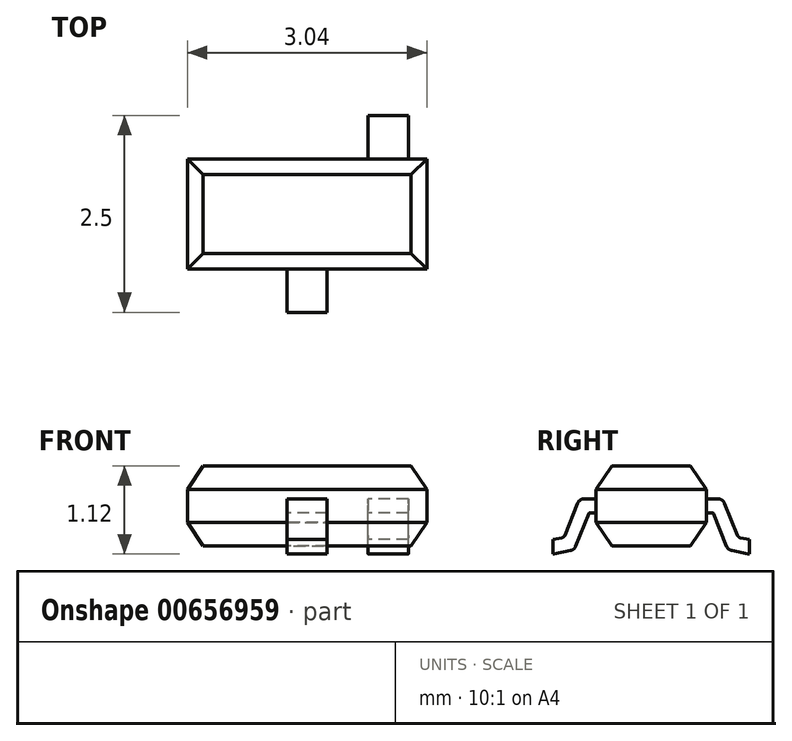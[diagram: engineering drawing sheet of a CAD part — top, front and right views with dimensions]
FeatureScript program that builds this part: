
annotation { "Feature Type Name" : "Feature", "Feature Type Description" : "" }
export const myFeature = defineFeature(function(context is Context, id is Id, definition is map)
    precondition{}
    {
        {
            var Q0;
            Q0=qCreatedBy(makeId("Top.planeOp"),FACE);
            cPlane(context, id + "F0", {"entities" : qUnion([Q0]), "cplaneType" : CPlaneType.OFFSET, "offset" : 0.1 * mm, "width" : 150 * mm, "height" : 150 * mm});
        }
        {
            var Q0;
            Q0=qCreatedBy(id+"F0.planeOp",FACE);
            var sketch = newSketch(context, id + "F1", { "sketchPlane" : qUnion([Q0])});
            skLineSegment(sketch, "E0.bottom", {"start": v(-1.52, 0.7) * mm, "end": v(1.52, 0.7) * mm});
            skLineSegment(sketch, "E0.top", {"start": v(-1.52, -0.7) * mm, "end": v(1.52, -0.7) * mm});
            skLineSegment(sketch, "E0.left", {"start": v(-1.52, 0.7) * mm, "end": v(-1.52, -0.7) * mm});
            skLineSegment(sketch, "E0.right", {"start": v(1.52, 0.7) * mm, "end": v(1.52, -0.7) * mm});
            skPoint(sketch, "E0.middle", {"position": v(0, 0) * mm});
            skSolve(sketch);
        }
        {
            var Q0;
            Q0=makeQuery(id+"F1.imprint","IMPRINT",FACE,{"disambiguationData":[TD([[makeQuery(id+"F1.imprint","IMPRINT",EDGE,{"derivedFrom":sQuery(id+"F1.wireOp",EDGE,"E0.bottom")}),-1.0]])]});
            extrude(context, id + "F2", {"entities" : qUnion([Q0]), "depth" : 1.02 * mm, "offsetDistance" : 25 * mm});
        }
        {
            var Q0;
            Q0=makeQuery(id+"F2.opExtrude","CAP_EDGE",EDGE,{"disambiguationData":[OSD([sQuery(id+"F1.wireOp",EDGE,"E0.left")])],"isStart":false});
            var Q1;
            Q1=makeQuery(id+"F2.opExtrude","CAP_EDGE",EDGE,{"disambiguationData":[OSD([sQuery(id+"F1.wireOp",EDGE,"E0.left")])],"isStart":true});
            var Q2;
            Q2=makeQuery(id+"F2.opExtrude","CAP_EDGE",EDGE,{"disambiguationData":[OSD([sQuery(id+"F1.wireOp",EDGE,"E0.right")])],"isStart":true});
            var Q3;
            Q3=makeQuery(id+"F2.opExtrude","CAP_EDGE",EDGE,{"disambiguationData":[OSD([sQuery(id+"F1.wireOp",EDGE,"E0.right")])],"isStart":false});
            chamfer(context, id + "F3", {"entities" : qUnion([Q0, Q1, Q2, Q3]), "chamferType" : ChamferType.TWO_OFFSETS, "width1" : 0.2 * mm, "oppositeDirection" : false, "width2" : 0.3 * mm, "tangentPropagation" : true});
        }
        {
            var Q0;
            Q0=makeQuery(id+"F2.opExtrude","CAP_EDGE",EDGE,{"disambiguationData":[OSD([sQuery(id+"F1.wireOp",EDGE,"E0.top")])],"isStart":false});
            var Q1;
            Q1=makeQuery(id+"F2.opExtrude","CAP_EDGE",EDGE,{"disambiguationData":[OSD([sQuery(id+"F1.wireOp",EDGE,"E0.top")])],"isStart":true});
            var Q2;
            Q2=makeQuery(id+"F2.opExtrude","CAP_EDGE",EDGE,{"disambiguationData":[OSD([sQuery(id+"F1.wireOp",EDGE,"E0.bottom")])],"isStart":true});
            var Q3;
            Q3=makeQuery(id+"F2.opExtrude","CAP_EDGE",EDGE,{"disambiguationData":[OSD([sQuery(id+"F1.wireOp",EDGE,"E0.bottom")])],"isStart":false});
            chamfer(context, id + "F4", {"entities" : qUnion([Q0, Q1, Q2, Q3]), "chamferType" : ChamferType.TWO_OFFSETS, "width1" : 0.2 * mm, "oppositeDirection" : false, "width2" : 0.3 * mm, "tangentPropagation" : true});
        }
        {
            var Q0;
            {var subQ0=sQuery(id+"F1.wireOp",EDGE,"E0.top");Q0=makeQuery(id+"F4.opChamfer","BLEND_EDGE",EDGE,{"blendedFrom":[makeQuery(id+"F2.opExtrude","CAP_EDGE",EDGE,{"disambiguationData":[OSD([subQ0])],"isStart":false}),makeQuery(id+"F2.opExtrude","CAP_FACE",FACE,{"disambiguationData":[OSD([sQuery(id+"F1.wireOp",EDGE,"E0.bottom"),subQ0,sQuery(id+"F1.wireOp",EDGE,"E0.left"),sQuery(id+"F1.wireOp",EDGE,"E0.right")])],"isStart":false})],"blendedInto":[makeQuery(id+"F2.opExtrude","CAP_FACE",FACE,{"disambiguationData":[OSD([sQuery(id+"F1.wireOp",EDGE,"E0.bottom"),subQ0,sQuery(id+"F1.wireOp",EDGE,"E0.left"),sQuery(id+"F1.wireOp",EDGE,"E0.right")])],"isStart":false})]});}
            cPoint(context, id + "F5", {"entities" : qUnion([Q0]), "parameter" : 0.5});
        }
        {
            var Q0;
            {var subQ0=sQuery(id+"F1.wireOp",EDGE,"E0.bottom");Q0=makeQuery(id+"F4.opChamfer","BLEND_EDGE",EDGE,{"blendedFrom":[makeQuery(id+"F2.opExtrude","CAP_EDGE",EDGE,{"disambiguationData":[OSD([subQ0])],"isStart":false}),makeQuery(id+"F2.opExtrude","CAP_FACE",FACE,{"disambiguationData":[OSD([subQ0,sQuery(id+"F1.wireOp",EDGE,"E0.top"),sQuery(id+"F1.wireOp",EDGE,"E0.left"),sQuery(id+"F1.wireOp",EDGE,"E0.right")])],"isStart":false})],"blendedInto":[makeQuery(id+"F2.opExtrude","CAP_FACE",FACE,{"disambiguationData":[OSD([subQ0,sQuery(id+"F1.wireOp",EDGE,"E0.top"),sQuery(id+"F1.wireOp",EDGE,"E0.left"),sQuery(id+"F1.wireOp",EDGE,"E0.right")])],"isStart":false})]});}
            cPoint(context, id + "F6", {"entities" : qUnion([Q0]), "parameter" : 0.5});
        }
        {
            var Q0;
            {var subQ0=sQuery(id+"F1.wireOp",EDGE,"E0.bottom");Q0=makeQuery(id+"F4.opChamfer","BLEND_EDGE",EDGE,{"blendedFrom":[makeQuery(id+"F2.opExtrude","CAP_EDGE",EDGE,{"disambiguationData":[OSD([subQ0])],"isStart":true}),makeQuery(id+"F2.opExtrude","CAP_FACE",FACE,{"disambiguationData":[OSD([subQ0,sQuery(id+"F1.wireOp",EDGE,"E0.top"),sQuery(id+"F1.wireOp",EDGE,"E0.left"),sQuery(id+"F1.wireOp",EDGE,"E0.right")])],"isStart":true})],"blendedInto":[makeQuery(id+"F2.opExtrude","CAP_FACE",FACE,{"disambiguationData":[OSD([subQ0,sQuery(id+"F1.wireOp",EDGE,"E0.top"),sQuery(id+"F1.wireOp",EDGE,"E0.left"),sQuery(id+"F1.wireOp",EDGE,"E0.right")])],"isStart":true})]});}
            cPoint(context, id + "F7", {"entities" : qUnion([Q0]), "parameter" : 0.5});
        }
        {
            var Q0;
            Q0=qCreatedBy(id+"F5",VERTEX);
            var Q1;
            Q1=qCreatedBy(id+"F6",VERTEX);
            var Q2;
            Q2=qCreatedBy(id+"F7",VERTEX);
            cPlane(context, id + "F8", {"entities" : qUnion([Q0, Q1, Q2]), "cplaneType" : CPlaneType.THREE_POINT, "offset" : 25 * mm, "width" : 150 * mm, "height" : 150 * mm});
        }
        {
            var Q0;
            Q0=qCreatedBy(id+"F8.planeOp",FACE);
            var sketch = newSketch(context, id + "F9", { "sketchPlane" : qUnion([Q0])});
            skLineSegment(sketch, "E1", {"start": v(0, 0) * mm, "end": v(-2.5, 0) * mm, "construction": true});
            skLineSegment(sketch, "E2", {"start": v(-1.25, 0) * mm, "end": v(-1.25, 0.09) * mm});
            skLineSegment(sketch, "E3", {"start": v(-0.7, 0.61) * mm, "end": v(-0.85, 0.61) * mm, "construction": true});
            skLineSegment(sketch, "E4", {"start": v(-1.04, 0.13) * mm, "end": v(-0.85, 0.61) * mm, "construction": true});
            skArc(sketch, "E5.0.startCap", {"start": v(-0.96, 0.1) * mm, "mid": v(-0.98, 0.06) * mm, "end": v(-1.02, 0.04) * mm});
            skArc(sketch, "E5.0.endCap", {"start": v(-0.93, 0.64) * mm, "mid": v(-0.9, 0.68) * mm, "end": v(-0.85, 0.7) * mm});
            skLineSegment(sketch, "E5.0.left", {"start": v(-1.1, 0.24) * mm, "end": v(-0.93, 0.64) * mm});
            skLineSegment(sketch, "E5.0.right", {"start": v(-0.96, 0.1) * mm, "end": v(-0.8, 0.51) * mm});
            skArc(sketch, "E6.0.startCap", {"start": v(-1.23, 0) * mm, "mid": v(-1.24, 0) * mm, "end": v(-1.25, 0) * mm});
            skLineSegment(sketch, "E6.0.left", {"start": v(-1.25, 0.18) * mm, "end": v(-1.13, 0.2) * mm});
            skLineSegment(sketch, "E6.0.right", {"start": v(-1.23, 0) * mm, "end": v(-1.02, 0.04) * mm});
            skLineSegment(sketch, "E6.1.left", {"start": v(-0.7, 0.52) * mm, "end": v(-0.78, 0.52) * mm});
            skLineSegment(sketch, "E6.1.right", {"start": v(-0.7, 0.7) * mm, "end": v(-0.85, 0.7) * mm});
            skLineSegment(sketch, "E7", {"start": v(-0.7, 0.7) * mm, "end": v(-0.7, 0.52) * mm});
            skLineSegment(sketch, "E8", {"start": v(-1.25, 0.18) * mm, "end": v(-1.25, 0.18) * mm});
            skLineSegment(sketch, "E9.trimOffspring", {"start": v(-1.25, 0.09) * mm, "end": v(-1.25, 0) * mm});
            skLineSegment(sketch, "E10", {"start": v(-1.25, 0.09) * mm, "end": v(-1.25, 0.18) * mm});
            skPoint(sketch, "E11.visualSharp", {"position": v(-0.79, 0.52) * mm});
            skArc(sketch, "E11.filletArc", {"start": v(-0.78, 0.52) * mm, "mid": v(-0.79, 0.52) * mm, "end": v(-0.8, 0.51) * mm});
            skPoint(sketch, "E12.visualSharp", {"position": v(-1.1, 0.21) * mm});
            skArc(sketch, "E12.filletArc", {"start": v(-1.13, 0.2) * mm, "mid": v(-1.11, 0.22) * mm, "end": v(-1.1, 0.24) * mm});
            skSolve(sketch);
        }
        {
            var Q0;
            Q0=makeQuery(id+"F9.imprint","IMPRINT",FACE,{"disambiguationData":[TD([[makeQuery(id+"F9.imprint","IMPRINT",EDGE,{"derivedFrom":sQuery(id+"F9.wireOp",EDGE,"E5.0.left")}),-1.0]])]});
            extrude(context, id + "F10", {"entities" : qUnion([Q0]), "operationType" : NewBodyOperationType.ADD, "endBound" : BoundingType.SYMMETRIC, "depth" : 0.51 * mm, "offsetDistance" : 25 * mm});
        }
        {
            var Q0;
            Q0=qCreatedBy(id+"F8.planeOp",FACE);
            cPlane(context, id + "F11", {"entities" : qUnion([Q0]), "cplaneType" : CPlaneType.OFFSET, "offset" : 1.03 * mm, "width" : 150 * mm, "height" : 150 * mm});
        }
        {
            var Q0;
            Q0=qCreatedBy(id+"F11.planeOp",FACE);
            var sketch = newSketch(context, id + "F12", { "sketchPlane" : qUnion([Q0])});
            skArc(sketch, "E13.MirrorCS", {"start": v(1.23, 0) * mm, "mid": v(1.24, 0) * mm, "end": v(1.25, 0) * mm});
            skArc(sketch, "E14.MirrorCS", {"start": v(0.78, 0.52) * mm, "mid": v(0.79, 0.52) * mm, "end": v(0.8, 0.51) * mm});
            skArc(sketch, "E15.MirrorCS", {"start": v(0.93, 0.64) * mm, "mid": v(0.9, 0.68) * mm, "end": v(0.85, 0.7) * mm});
            skArc(sketch, "E16.MirrorCS", {"start": v(0.96, 0.1) * mm, "mid": v(0.98, 0.06) * mm, "end": v(1.02, 0.04) * mm});
            skArc(sketch, "E17.MirrorCS", {"start": v(1.13, 0.2) * mm, "mid": v(1.11, 0.22) * mm, "end": v(1.1, 0.24) * mm});
            skLineSegment(sketch, "E18.MirrorCS", {"start": v(1.25, 0.18) * mm, "end": v(1.13, 0.2) * mm});
            skLineSegment(sketch, "E19.MirrorCS", {"start": v(0.7, 0.52) * mm, "end": v(0.78, 0.52) * mm});
            skLineSegment(sketch, "E20.MirrorCS", {"start": v(1.25, 0) * mm, "end": v(1.25, 0.18) * mm});
            skLineSegment(sketch, "E21.MirrorCS", {"start": v(1.23, 0) * mm, "end": v(1.02, 0.04) * mm});
            skLineSegment(sketch, "E22.MirrorCS", {"start": v(0.96, 0.1) * mm, "end": v(0.8, 0.51) * mm});
            skLineSegment(sketch, "E23.MirrorCS", {"start": v(0.7, 0.7) * mm, "end": v(0.85, 0.7) * mm});
            skLineSegment(sketch, "E24.MirrorCS", {"start": v(1.1, 0.24) * mm, "end": v(0.93, 0.64) * mm});
            skLineSegment(sketch, "E25", {"start": v(0.7, 0.7) * mm, "end": v(0.7, 0.52) * mm});
            skSolve(sketch);
        }
        {
            var Q0;
            Q0=qSketchRegion(id+"F12",true);
            extrude(context, id + "F13", {"entities" : qUnion([Q0]), "operationType" : NewBodyOperationType.ADD, "endBound" : BoundingType.SYMMETRIC, "depth" : 0.51 * mm, "offsetDistance" : 25 * mm});
        }
    });
